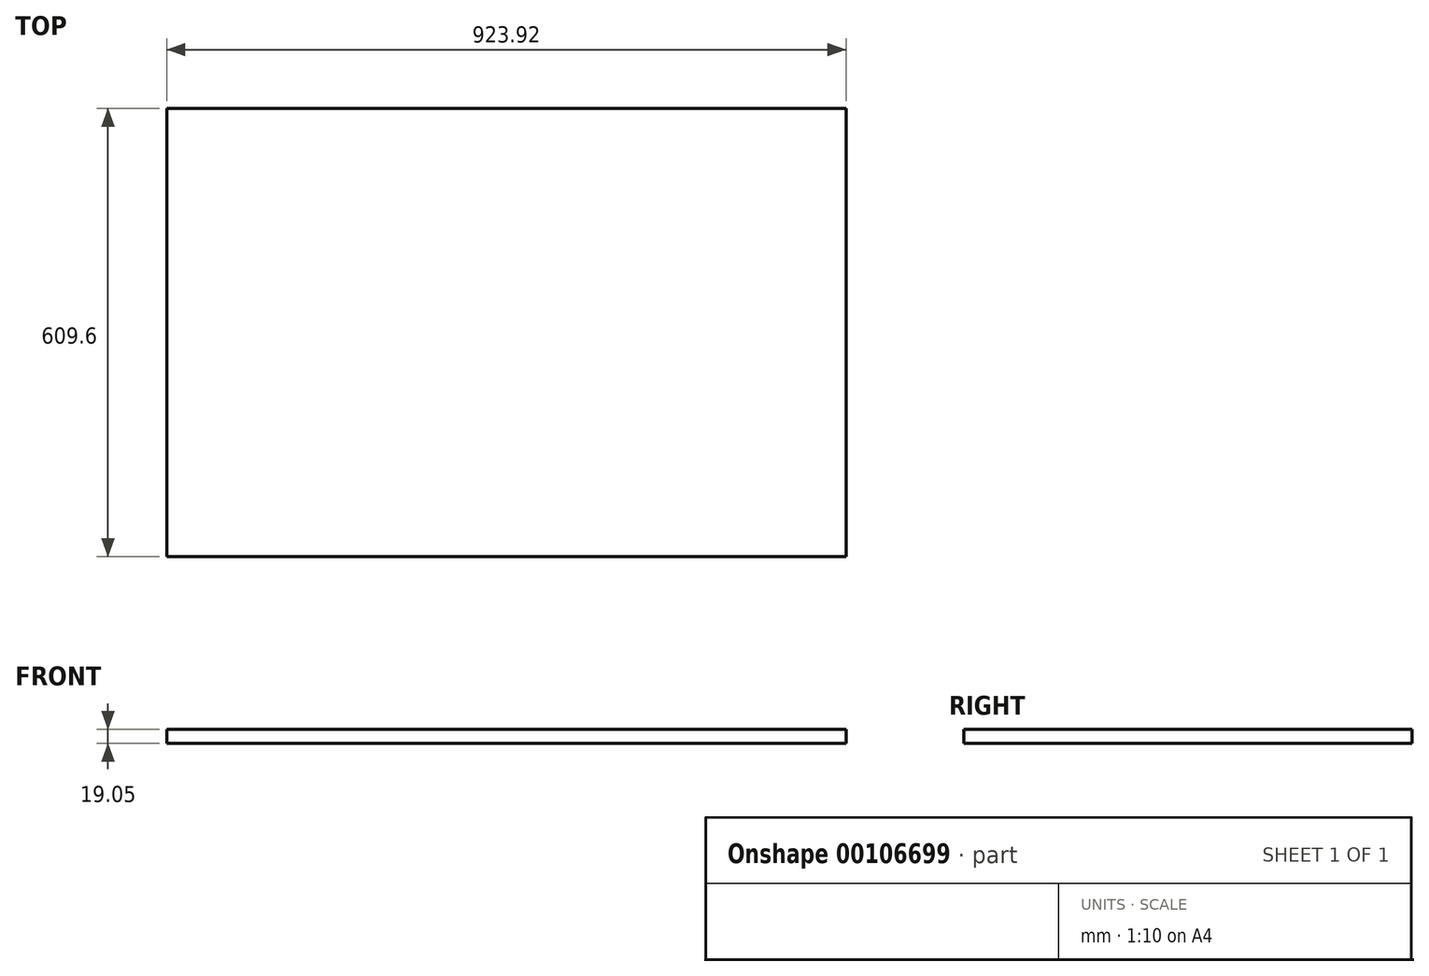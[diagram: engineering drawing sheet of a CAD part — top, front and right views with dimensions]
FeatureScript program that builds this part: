
annotation { "Feature Type Name" : "Feature", "Feature Type Description" : "" }
export const myFeature = defineFeature(function(context is Context, id is Id, definition is map)
    precondition{}
    {
        {
            var Q0;
            Q0=qCreatedBy(makeId("Top.planeOp"),FACE);
            var sketch = newSketch(context, id + "F0", { "sketchPlane" : qUnion([Q0])});
            skLineSegment(sketch, "E0.bottom", {"start": v(0, 0) * mm, "end": v(923.93, 0) * mm});
            skLineSegment(sketch, "E0.top", {"start": v(0, 609.6) * mm, "end": v(923.92, 609.6) * mm});
            skLineSegment(sketch, "E0.left", {"start": v(0, 0) * mm, "end": v(0, 609.6) * mm});
            skLineSegment(sketch, "E0.right", {"start": v(923.93, 0) * mm, "end": v(923.92, 609.6) * mm});
            skSolve(sketch);
        }
        {
            var Q0;
            Q0=makeQuery(id+"F0.imprint","IMPRINT",FACE,{"disambiguationData":[TD([[makeQuery(id+"F0.imprint","IMPRINT",EDGE,{"derivedFrom":sQuery(id+"F0.wireOp",EDGE,"E0.bottom")}),1.0]])]});
            extrude(context, id + "F1", {"entities" : qUnion([Q0]), "depth" : 19.05 * mm});
        }
    });
